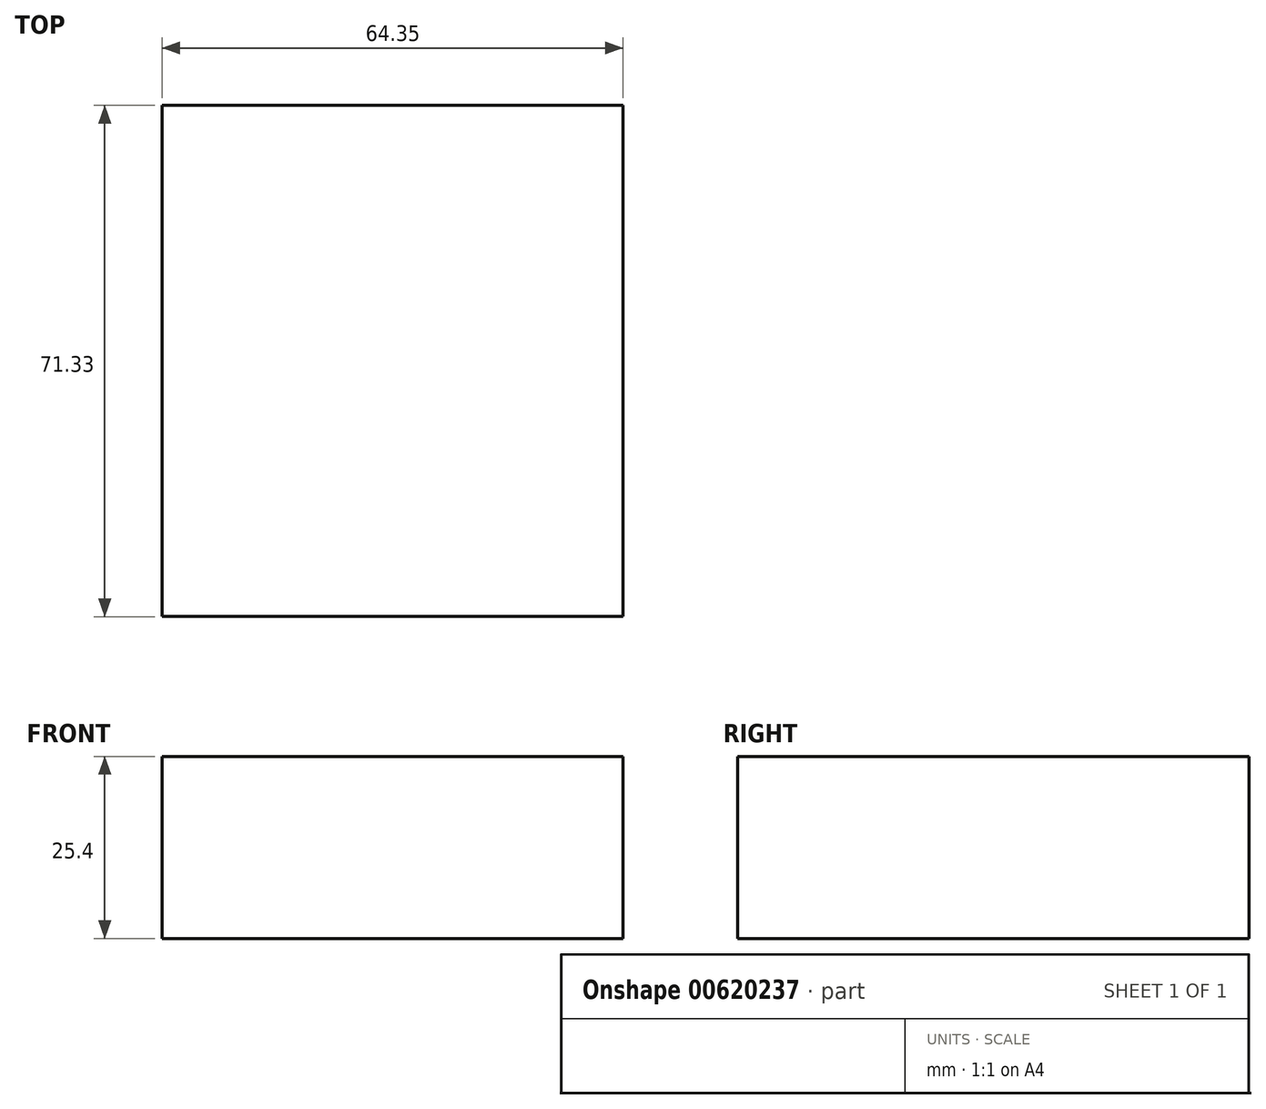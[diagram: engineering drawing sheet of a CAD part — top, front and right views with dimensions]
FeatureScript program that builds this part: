
annotation { "Feature Type Name" : "Feature", "Feature Type Description" : "" }
export const myFeature = defineFeature(function(context is Context, id is Id, definition is map)
    precondition{}
    {
        {
            var Q0;
            Q0=qCreatedBy(makeId("Top.planeOp"),FACE);
            var sketch = newSketch(context, id + "F0", { "sketchPlane" : qUnion([Q0])});
            skLineSegment(sketch, "E0.bottom", {"start": v(0, 0) * mm, "end": v(64.35, 0) * mm});
            skLineSegment(sketch, "E0.top", {"start": v(0, -71.33) * mm, "end": v(64.35, -71.33) * mm});
            skLineSegment(sketch, "E0.left", {"start": v(0, 0) * mm, "end": v(0, -71.33) * mm});
            skLineSegment(sketch, "E0.right", {"start": v(64.35, 0) * mm, "end": v(64.35, -71.33) * mm});
            skSolve(sketch);
        }
        {
            var Q0;
            Q0=makeQuery(id+"F0.imprint","IMPRINT",FACE,{"disambiguationData":[TD([[makeQuery(id+"F0.imprint","IMPRINT",EDGE,{"derivedFrom":sQuery(id+"F0.wireOp",EDGE,"E0.bottom")}),-1.0]])]});
            extrude(context, id + "F1", {"entities" : qUnion([Q0]), "depth" : 25.4 * mm, "offsetDistance" : 25.4 * mm});
        }
    });
